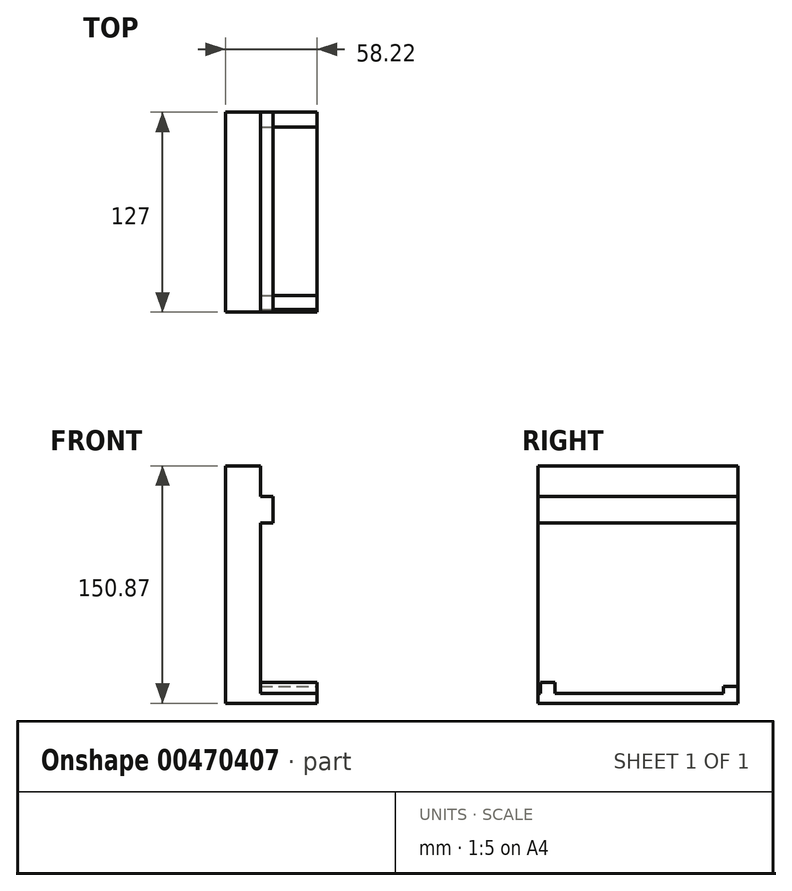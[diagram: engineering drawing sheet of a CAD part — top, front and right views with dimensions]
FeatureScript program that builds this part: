
annotation { "Feature Type Name" : "Feature", "Feature Type Description" : "" }
export const myFeature = defineFeature(function(context is Context, id is Id, definition is map)
    precondition{}
    {
        {
            var Q0;
            Q0=qCreatedBy(makeId("Front.planeOp"),FACE);
            var sketch = newSketch(context, id + "F0", { "sketchPlane" : qUnion([Q0])});
            skLineSegment(sketch, "E0.bottom", {"start": v(-58.22, 75.13) * mm, "end": v(-35.97, 75.13) * mm});
            skLineSegment(sketch, "E0.top", {"start": v(-58.22, -75.74) * mm, "end": v(-35.97, -75.74) * mm});
            skLineSegment(sketch, "E0.left", {"start": v(-58.22, 75.13) * mm, "end": v(-58.22, -75.74) * mm});
            skLineSegment(sketch, "E0.right", {"start": v(-35.97, 75.13) * mm, "end": v(-35.97, -75.74) * mm});
            skLineSegment(sketch, "E1.bottom", {"start": v(-35.97, 55.63) * mm, "end": v(-28.04, 55.63) * mm});
            skLineSegment(sketch, "E1.top", {"start": v(-35.97, 38.86) * mm, "end": v(-28.04, 38.86) * mm});
            skLineSegment(sketch, "E1.left", {"start": v(-35.97, 55.63) * mm, "end": v(-35.97, 38.86) * mm});
            skLineSegment(sketch, "E1.right", {"start": v(-28.04, 55.63) * mm, "end": v(-28.04, 38.86) * mm});
            skLineSegment(sketch, "E2.bottom", {"start": v(-35.97, -69.34) * mm, "end": v(0, -69.34) * mm});
            skLineSegment(sketch, "E2.top", {"start": v(-35.97, -75.74) * mm, "end": v(0, -75.74) * mm});
            skLineSegment(sketch, "E2.left", {"start": v(-35.97, -69.34) * mm, "end": v(-35.97, -75.74) * mm});
            skLineSegment(sketch, "E2.right", {"start": v(0, -69.34) * mm, "end": v(0, -75.74) * mm});
            skSolve(sketch);
        }
        {
            var Q0;
            Q0 = qSketchRegion(id + "F0", true);
            extrude(context, id + "F1", {"entities" : qUnion([Q0]), "depth" : 127 * mm});
        }
        {
            var Q0;
            Q0=qCreatedBy(makeId("Right.planeOp"),FACE);
            var sketch = newSketch(context, id + "F2", { "sketchPlane" : qUnion([Q0])});
            skLineSegment(sketch, "E3.bottom", {"start": v(-125.37, -75.74) * mm, "end": v(-116.23, -75.74) * mm});
            skLineSegment(sketch, "E3.top", {"start": v(-125.37, -62.33) * mm, "end": v(-116.23, -62.33) * mm});
            skLineSegment(sketch, "E3.left", {"start": v(-125.37, -75.74) * mm, "end": v(-125.37, -62.33) * mm});
            skLineSegment(sketch, "E3.right", {"start": v(-116.23, -75.74) * mm, "end": v(-116.23, -62.33) * mm});
            skLineSegment(sketch, "E4.bottom", {"start": v(0, -74.83) * mm, "end": v(-9.25, -74.83) * mm});
            skLineSegment(sketch, "E4.top", {"start": v(0, -65.07) * mm, "end": v(-9.25, -65.07) * mm});
            skLineSegment(sketch, "E4.left", {"start": v(0, -74.83) * mm, "end": v(0, -65.07) * mm});
            skLineSegment(sketch, "E4.right", {"start": v(-9.25, -74.83) * mm, "end": v(-9.25, -65.07) * mm});
            skSolve(sketch);
        }
        {
            var Q0;
            Q0 = qSketchRegion(id + "F2", true);
            extrude(context, id + "F3", {"entities" : qUnion([Q0]), "operationType" : NewBodyOperationType.ADD, "oppositeDirection" : true, "depth" : 51.56 * mm});
        }
    });
